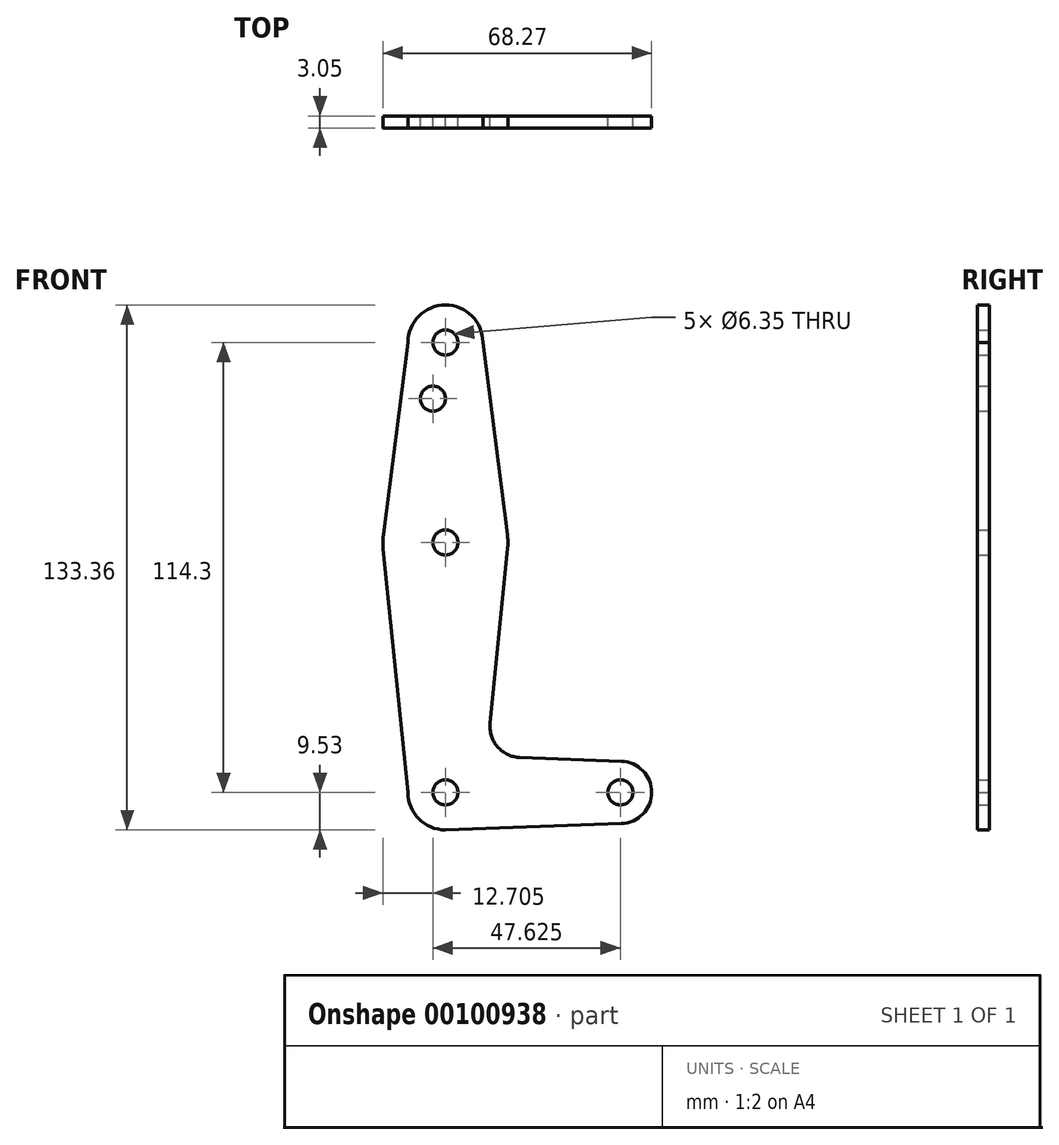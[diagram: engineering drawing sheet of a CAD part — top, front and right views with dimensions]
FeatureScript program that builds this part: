
annotation { "Feature Type Name" : "Feature", "Feature Type Description" : "" }
export const myFeature = defineFeature(function(context is Context, id is Id, definition is map)
    precondition{}
    {
        {
            var Q0;
            Q0=qCreatedBy(makeId("Front.planeOp"),FACE);
            var sketch = newSketch(context, id + "F0", { "sketchPlane" : qUnion([Q0])});
            skLineSegment(sketch, "E0", {"start": v(0, 0) * mm, "end": v(0, 114.3) * mm, "construction": true});
            skLineSegment(sketch, "E1", {"start": v(0, 0) * mm, "end": v(44.45, 0) * mm, "construction": true});
            skCircle(sketch, "E2", {"center": v(0, 114.3) * mm, "radius": 9.53 * mm});
            skCircle(sketch, "E3", {"center": v(0, 63.5) * mm, "radius": 15.88 * mm});
            skCircle(sketch, "E4", {"center": v(0, 0) * mm, "radius": 9.53 * mm});
            skCircle(sketch, "E5", {"center": v(44.45, 0) * mm, "radius": 7.94 * mm});
            skLineSegment(sketch, "E6", {"start": v(-15.75, 65.5) * mm, "end": v(-9.53, 114.3) * mm});
            skLineSegment(sketch, "E7", {"start": v(15.75, 65.5) * mm, "end": v(9.52, 114.3) * mm});
            skLineSegment(sketch, "E8", {"start": v(-15.8, 61.9) * mm, "end": v(-9.53, 0) * mm});
            skLineSegment(sketch, "E9", {"start": v(15.8, 61.91) * mm, "end": v(11.34, 17.6) * mm});
            skLineSegment(sketch, "E10", {"start": v(44.73, 7.93) * mm, "end": v(18.97, 8.85) * mm});
            skLineSegment(sketch, "E11", {"start": v(44.73, -7.93) * mm, "end": v(0, -9.53) * mm});
            skCircle(sketch, "E12", {"center": v(0, 114.3) * mm, "radius": 3.18 * mm});
            skCircle(sketch, "E13", {"center": v(0, 63.5) * mm, "radius": 3.18 * mm});
            skCircle(sketch, "E14", {"center": v(0, 0) * mm, "radius": 3.18 * mm});
            skCircle(sketch, "E15", {"center": v(44.45, 0) * mm, "radius": 3.18 * mm});
            skCircle(sketch, "E16", {"center": v(-3.18, 100.03) * mm, "radius": 3.18 * mm});
            skPoint(sketch, "E17.newPointB", {"position": v(9.57, 0) * mm});
            skArc(sketch, "E17.filletArc", {"start": v(11.34, 17.6) * mm, "mid": v(13.26, 11.57) * mm, "end": v(18.97, 8.85) * mm});
            skSolve(sketch);
        }
        {
            var Q0;
            {var subQ1=sQuery(id+"F0.wireOp",EDGE,"E6");Q0=makeQuery(id+"F0.imprint","IMPRINT",FACE,{"disambiguationData":[TD([[makeQuery(id+"F0.imprint","IMPRINT",EDGE,{"derivedFrom":subQ1}),-1.0]])]});}
            var Q1;
            Q1=makeQuery(id+"F0.imprint","IMPRINT",FACE,{"disambiguationData":[TD([[makeQuery(id+"F0.imprint","IMPRINT",EDGE,{"derivedFrom":sQuery(id+"F0.wireOp",EDGE,"E12")}),-1.0]])]});
            var Q2;
            Q2=makeQuery(id+"F0.imprint","IMPRINT",FACE,{"disambiguationData":[TD([[makeQuery(id+"F0.imprint","IMPRINT",EDGE,{"derivedFrom":sQuery(id+"F0.wireOp",EDGE,"E13")}),-1.0]])]});
            var Q3;
            {var subQ0=sQuery(id+"F0.wireOp",EDGE,"E8");Q3=makeQuery(id+"F0.imprint","IMPRINT",FACE,{"disambiguationData":[TD([[makeQuery(id+"F0.imprint","IMPRINT",EDGE,{"derivedFrom":subQ0}),1.0]])]});}
            var Q4;
            Q4=makeQuery(id+"F0.imprint","IMPRINT",FACE,{"disambiguationData":[TD([[makeQuery(id+"F0.imprint","IMPRINT",EDGE,{"derivedFrom":sQuery(id+"F0.wireOp",EDGE,"E14")}),-1.0]])]});
            var Q5;
            Q5=makeQuery(id+"F0.imprint","IMPRINT",FACE,{"disambiguationData":[TD([[makeQuery(id+"F0.imprint","IMPRINT",EDGE,{"derivedFrom":sQuery(id+"F0.wireOp",EDGE,"E15")}),-1.0]])]});
            extrude(context, id + "F1", {"entities" : qUnion([Q0, Q1, Q2, Q3, Q4, Q5]), "depth" : 3.05 * mm});
        }
    });
